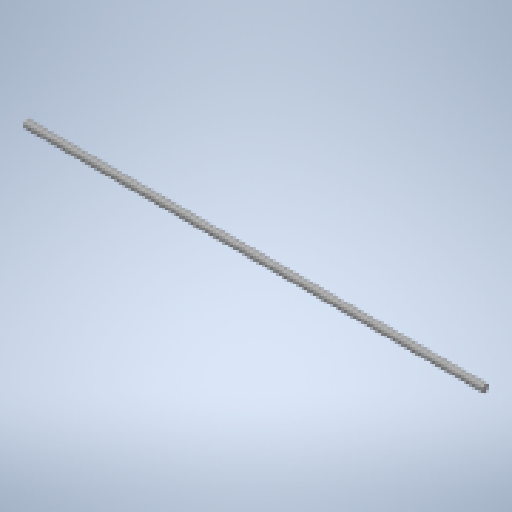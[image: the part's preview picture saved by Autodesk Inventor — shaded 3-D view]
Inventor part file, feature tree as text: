
AUTODESK INVENTOR PART (.ipt)
format: ipt  version: 2023 (Build 270158000, 158)  size: 131,072 bytes
history: native  units: mm
features: other x3, revolve x1
ambient origin geometry x6: Origin, XZ Plane, XY Plane, X Axis, Y Axis, Z Axis
bodies: Solid1 (feature_tree)
feature tree (4):
  revolve  "Revolution1"  [1 undecoded]
  other  "Start Plane"
  other  "Origin point"
  other  "Main Sketch"
note: 1 required parameter value undecoded (feature->parameter linkage not recoverable at this tier; creation-order binding heuristic only, values carry confidence <= 0.55)
